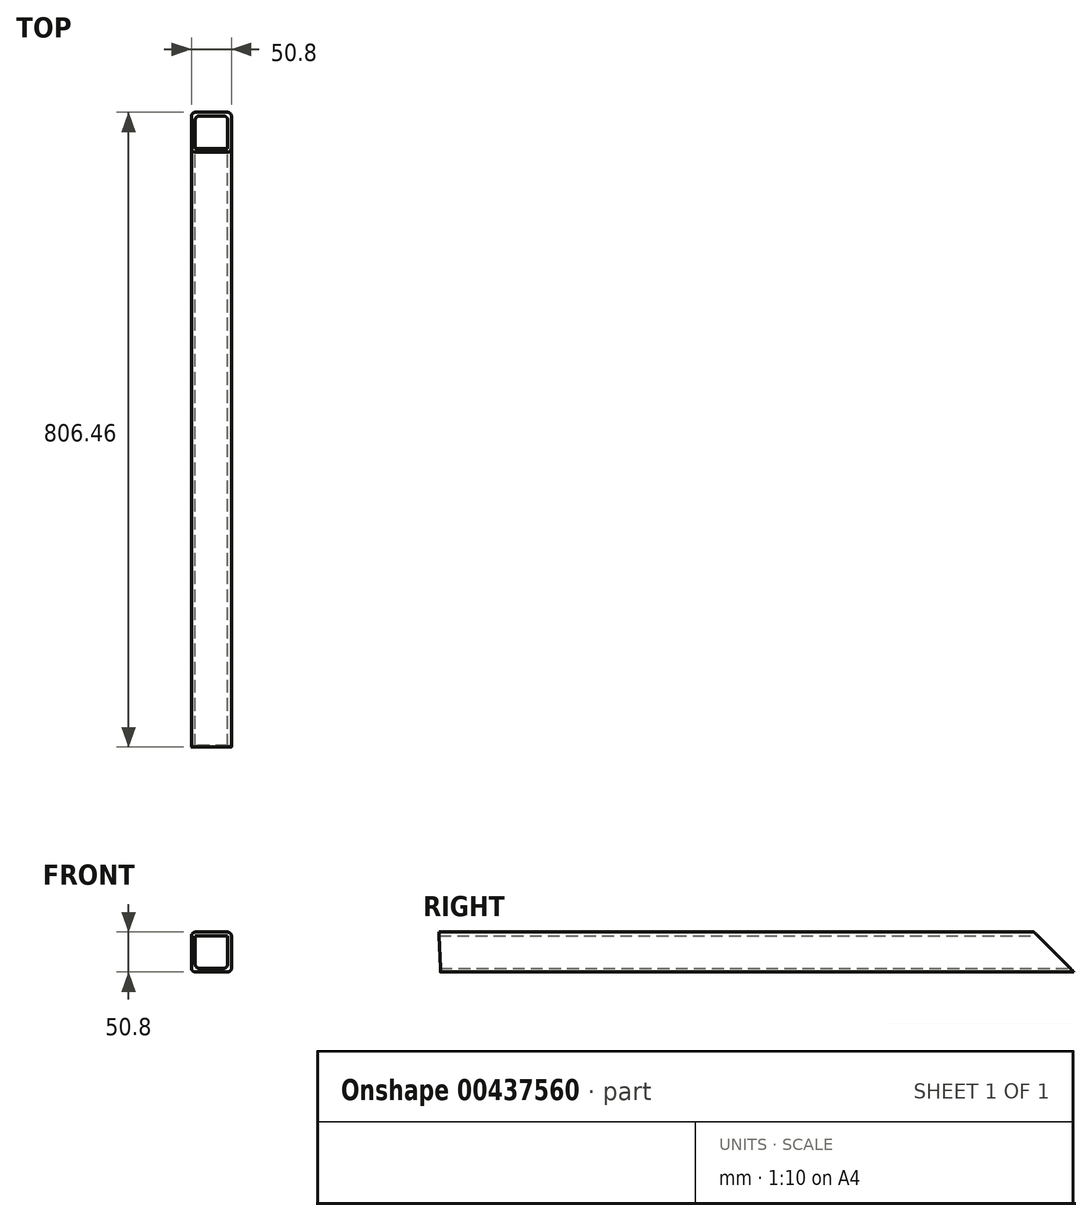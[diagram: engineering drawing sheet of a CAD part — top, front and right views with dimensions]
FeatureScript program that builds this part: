
annotation { "Feature Type Name" : "Feature", "Feature Type Description" : "" }
export const myFeature = defineFeature(function(context is Context, id is Id, definition is map)
    precondition{}
    {
        {
            var Q0;
            Q0=qCreatedBy(makeId("Front.planeOp"),FACE);
            var sketch = newSketch(context, id + "F0", { "sketchPlane" : qUnion([Q0])});
            skLineSegment(sketch, "E0.bottom", {"start": v(25.4, -25.4) * mm, "end": v(-25.4, -25.4) * mm});
            skLineSegment(sketch, "E0.top", {"start": v(25.4, 25.4) * mm, "end": v(-25.4, 25.4) * mm});
            skLineSegment(sketch, "E0.left", {"start": v(25.4, -25.4) * mm, "end": v(25.4, 25.4) * mm});
            skLineSegment(sketch, "E0.right", {"start": v(-25.4, -25.4) * mm, "end": v(-25.4, 25.4) * mm});
            skPoint(sketch, "E0.middle", {"position": v(0, 0) * mm});
            skLineSegment(sketch, "E1.bottom", {"start": v(20.64, -20.64) * mm, "end": v(-20.64, -20.64) * mm});
            skLineSegment(sketch, "E1.top", {"start": v(20.64, 20.64) * mm, "end": v(-20.64, 20.64) * mm});
            skLineSegment(sketch, "E1.left", {"start": v(20.64, -20.64) * mm, "end": v(20.64, 20.64) * mm});
            skLineSegment(sketch, "E1.right", {"start": v(-20.64, -20.64) * mm, "end": v(-20.64, 20.64) * mm});
            skSolve(sketch);
        }
        {
            var Q0;
            Q0 = qSketchRegion(id + "F0", true);
            extrude(context, id + "F1", {"entities" : qUnion([Q0]), "endBound" : BoundingType.SYMMETRIC, "depth" : 806.45 * mm});
        }
        {
            var Q0;
            Q0=makeQuery(id+"F1.opExtrude","SWEPT_FACE",FACE,{"disambiguationData":[OSD([sQuery(id+"F0.wireOp",EDGE,"E0.right")])]});
            var sketch = newSketch(context, id + "F2", { "sketchPlane" : qUnion([Q0])});
            skLineSegment(sketch, "E2", {"start": v(-403.23, 25.4) * mm, "end": v(-403.23, -25.4) * mm});
            skLineSegment(sketch, "E3", {"start": v(-403.23, -25.4) * mm, "end": v(-289.25, 88.58) * mm});
            skLineSegment(sketch, "E4", {"start": v(403.23, 25.4) * mm, "end": v(403.23, -25.4) * mm});
            skLineSegment(sketch, "E5", {"start": v(403.23, -25.4) * mm, "end": v(403.23, 25.4) * mm});
            skLineSegment(sketch, "E6", {"start": v(403.23, 25.4) * mm, "end": v(397.09, -150.41) * mm});
            skSolve(sketch);
        }
        {
            var Q0;
            Q0 = qSketchRegion(id + "F2", true);
            var Q1;
            {var subQ0=sQuery(id+"F2.wireOp",EDGE,"E2");Q1=makeQuery(id+"F2.imprint","IMPRINT",FACE,{"disambiguationData":[TD([[makeQuery(id+"F2.imprint","IMPRINT",EDGE,{"derivedFrom":subQ0}),-1.0]])]});}
            var Q2;
            {var subQ0=sQuery(id+"F2.wireOp",EDGE,"E4");Q2=makeQuery(id+"F2.imprint","IMPRINT",FACE,{"disambiguationData":[TD([[makeQuery(id+"F2.imprint","IMPRINT",EDGE,{"derivedFrom":subQ0}),1.0]])]});}
            extrude(context, id + "F3", {"entities" : qUnion([Q0, Q1, Q2]), "operationType" : NewBodyOperationType.REMOVE, "oppositeDirection" : true, "depth" : 50.8 * mm});
        }
        {
            var Q0;
            Q0=makeQuery(id+"F1.opExtrude","SWEPT_EDGE",EDGE,{"disambiguationData":[OSD([sQuery(id+"F0.wireOp",EDGE,"E0.top"),sQuery(id+"F0.wireOp",EDGE,"E0.right")])]});
            var Q1;
            Q1=makeQuery(id+"F1.opExtrude","SWEPT_EDGE",EDGE,{"disambiguationData":[OSD([sQuery(id+"F0.wireOp",EDGE,"E0.top"),sQuery(id+"F0.wireOp",EDGE,"E0.left")])]});
            var Q2;
            Q2=makeQuery(id+"F1.opExtrude","SWEPT_EDGE",EDGE,{"disambiguationData":[OSD([sQuery(id+"F0.wireOp",EDGE,"E1.bottom"),sQuery(id+"F0.wireOp",EDGE,"E1.left")])]});
            var Q3;
            Q3=makeQuery(id+"F1.opExtrude","SWEPT_EDGE",EDGE,{"disambiguationData":[OSD([sQuery(id+"F0.wireOp",EDGE,"E1.bottom"),sQuery(id+"F0.wireOp",EDGE,"E1.right")])]});
            var Q4;
            Q4=makeQuery(id+"F1.opExtrude","SWEPT_EDGE",EDGE,{"disambiguationData":[OSD([sQuery(id+"F0.wireOp",EDGE,"E0.bottom"),sQuery(id+"F0.wireOp",EDGE,"E0.right")])]});
            var Q5;
            Q5=makeQuery(id+"F1.opExtrude","SWEPT_EDGE",EDGE,{"disambiguationData":[OSD([sQuery(id+"F0.wireOp",EDGE,"E0.bottom"),sQuery(id+"F0.wireOp",EDGE,"E0.left")])]});
            fillet(context, id + "F4", {"entities" : qUnion([Q0, Q1, Q2, Q3, Q4, Q5]), "radius" : 5.08 * mm, "tangentPropagation" : true, "allowEdgeOverflow" : false});
        }
    });
